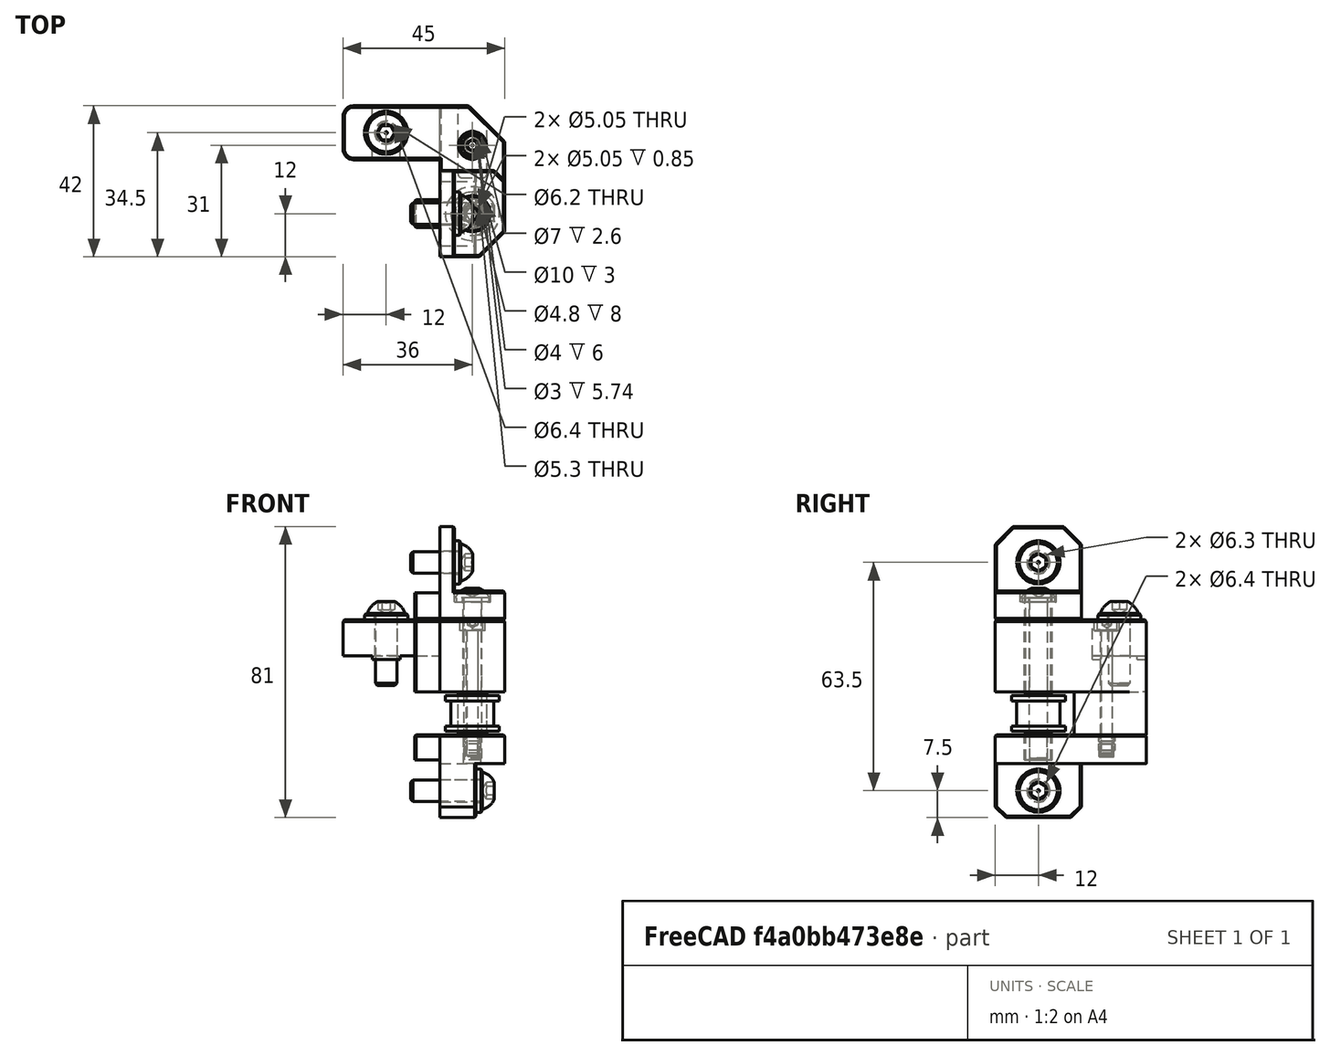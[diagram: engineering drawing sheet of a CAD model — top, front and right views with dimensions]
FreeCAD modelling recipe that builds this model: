
FCSTD DOCUMENT  (FreeCAD 0.19R24291 (Git))
Label: front-left-idler-assembly
License: Other
LicenseURL: GPL3
objects: Part::FeaturePython×10, Part::Feature×6, PartDesign::CoordinateSystem×1, App::Part×1
note: 17 computed .brp shape members not serialized (recipe doc carries the construction recipe); baked Part::Feature solids carry a one-line shape summary decoded from their .brp

FEATURE [Part::Feature] Cut002002002002001  label="front-idler-spacer"
  Placement = pos=(-2,0,0) rot=(0,0,1;0rad)
  shape: bbox 8 x 8 x 0.85 mm, 4 faces (baked)
FEATURE [Part::Feature] Cut002002002001001  label="front-idler-spacer001"
  Placement = pos=(-2,0,0) rot=(0,0,1;0rad)
  shape: bbox 8 x 8 x 0.85 mm, 4 faces (baked)
FEATURE [Part::Feature] Cut002002002003  label="smooth-idler-6mm002"
  Placement = pos=(-2,0,0) rot=(0,0,1;0rad)
  shape: bbox 15 x 15 x 10 mm, 8 faces (baked)
FEATURE [Part::FeaturePython] Washer002  label="M6-Washer006"  # Fasteners workbench fastener (typed FeaturePython)
  Placement = pos=(-15,37.5,40) rot=(0,0,1;0rad)
  diameter = 2
  invert = false
  matchOuter = true
  offset = 0
  type = 4
FEATURE [Part::FeaturePython] Screw006  label="M3x35-Screw"  # Fasteners workbench fastener (typed FeaturePython)
  Placement = pos=(9,34,37) rot=(0,0,1;0rad)
  diameter = 4
  invert = false
  length = 10
  lengthCustom = 35
  matchOuter = true
  offset = 0
  thread = false
  type = 33
FEATURE [Part::FeaturePython] Screw011  label="M6x20-Screw001"  # Fasteners workbench fastener (typed FeaturePython)
  Placement = pos=(-15,37.5,41.8) rot=(0,0,1;0rad)
  baseObject = -> Washer002 [Edge1]
  diameter = 4
  invert = false
  length = 4
  lengthCustom = 20
  matchOuter = true
  offset = 0
  thread = false
  type = 39
FEATURE [Part::FeaturePython] Washer007  label="M5-Washer"  # Fasteners workbench fastener (typed FeaturePython)
  Placement = pos=(9,15,45) rot=(0,0,1;0rad)
  diameter = 6
  invert = false
  matchOuter = true
  offset = 0
  type = 5
FEATURE [Part::FeaturePython] Screw013  label="M5x45-Screw"  # Fasteners workbench fastener (typed FeaturePython)
  Placement = pos=(9,15,46.1) rot=(0,0,1;0rad)
  baseObject = -> Washer007 [Edge1]
  diameter = 3
  invert = false
  length = 10
  lengthCustom = 45
  matchOuter = true
  offset = 0
  thread = false
  type = 39
FEATURE [Part::FeaturePython] HeatSet  label="M3x4-HeatSet"  # WARN: FeaturePython — macro-defined, semantics opaque (R4)
  Placement = pos=(9,34,8) rot=(0,0,1;0rad)
  diameter = 2
  invert = false
  offset = 0
FEATURE [Part::FeaturePython] Washer008  label="M6-Washer007"  # Fasteners workbench fastener (typed FeaturePython)
  Placement = pos=(4,15,56) rot=(0,1,0;1.5708rad)
  diameter = 2
  invert = true
  matchOuter = true
  offset = 0
  type = 4
FEATURE [Part::FeaturePython] Washer009  label="M6-Washer"  # Fasteners workbench fastener (typed FeaturePython)
  Placement = pos=(10,15,-7.5) rot=(0,1,0;1.5708rad)
  diameter = 2
  invert = false
  matchOuter = true
  offset = 0
  type = 4
FEATURE [Part::FeaturePython] Screw014  label="M6x14-Screw"  # Fasteners workbench fastener (typed FeaturePython)
  Placement = pos=(5.8,15,56) rot=(0,1,0;1.5708rad)
  baseObject = -> Washer008 [Edge1]
  diameter = 4
  invert = false
  length = 2
  lengthCustom = 14
  matchOuter = true
  offset = 0
  thread = false
  type = 40
FEATURE [Part::FeaturePython] Screw015  label="M6x20-Screw"  # Fasteners workbench fastener (typed FeaturePython)
  Placement = pos=(11.8,15,-7.5) rot=(0,1,0;1.5708rad)
  baseObject = -> Washer009 [Edge1]
  diameter = 4
  invert = false
  length = 4
  lengthCustom = 20
  matchOuter = true
  offset = 0
  thread = false
  type = 40
FEATURE [PartDesign::CoordinateSystem] LCS_left_idler  label="LCS_left-idler"
  AttacherType = Attacher::AttachEngine3D
FEATURE [Part::Feature] Cut002002002007004004001006001001  label="left-idler-bottom"
  shape: bbox 25 x 42 x 23 mm, 49 faces (baked)
FEATURE [Part::Feature] Cut002002002007004004001003001001  label="left-idler-mid"
  shape: bbox 45 x 42 x 32 mm, 65 faces (baked)
FEATURE [Part::Feature] Cut002002002007004004001005001001  label="left-idler-top"
  shape: bbox 25 x 24 x 26 mm, 64 faces (baked)
FEATURE [App::Part] Part  label="left-idler"
  Group = -> [Cut002002002002001,Cut002002002001001,Cut002002002003,Screw006,Washer002,Screw011,Screw013,Washer007,HeatSet,Washer008,Washer009,Screw014,Screw015,LCS_left_idler,Cut002002002007004004001006001001,Cut002002002007004004001003001001,Cut002002002007004004001005001001]
  Origin = -> Origin
